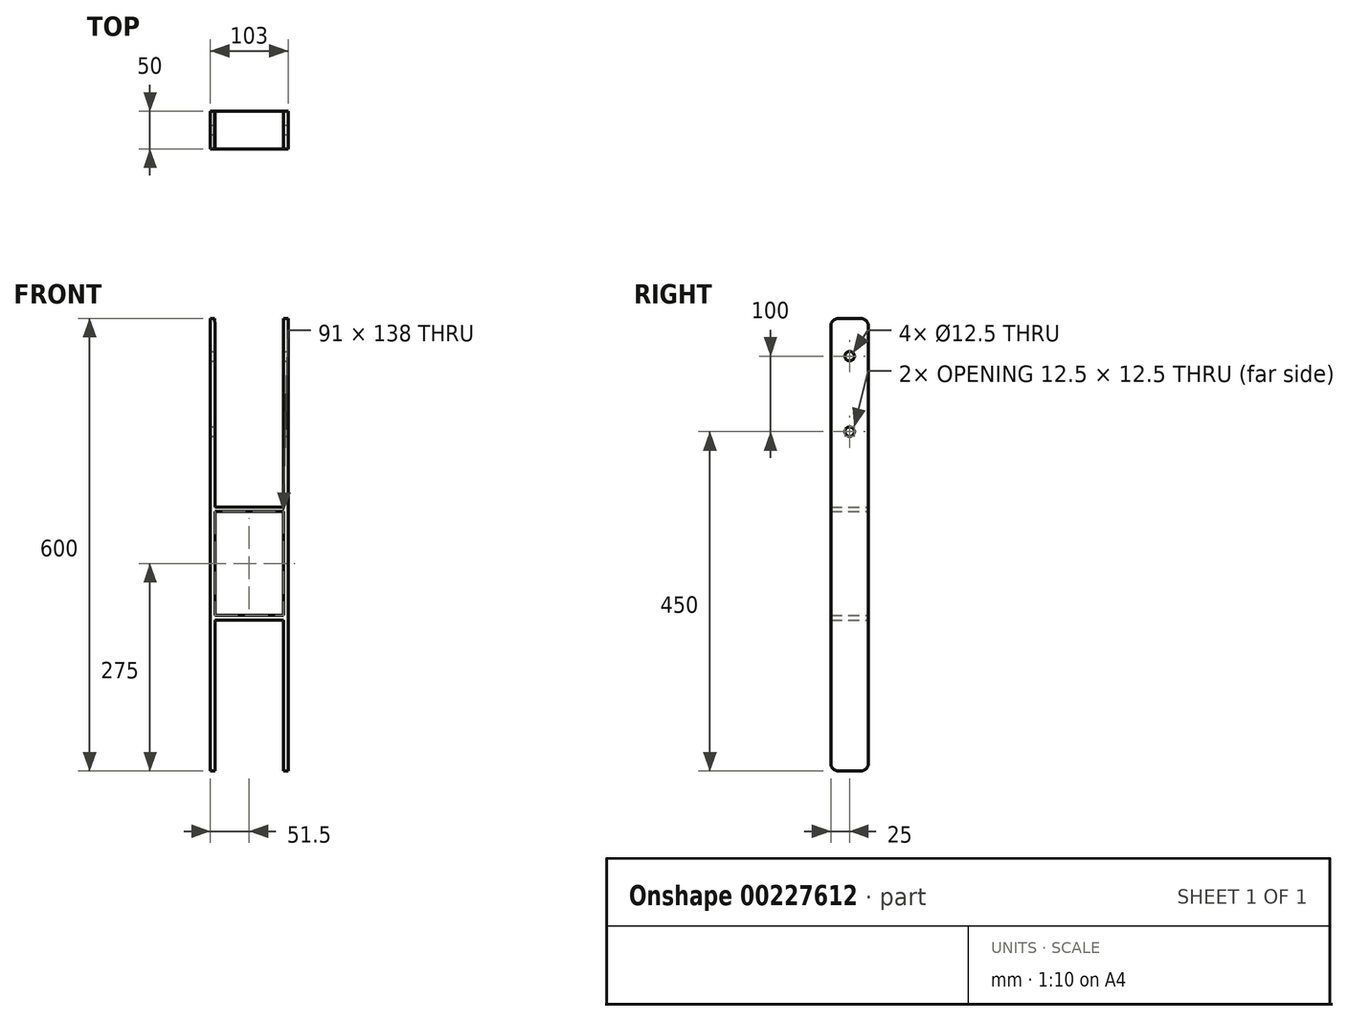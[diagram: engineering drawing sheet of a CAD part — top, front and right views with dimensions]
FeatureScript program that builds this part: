
annotation { "Feature Type Name" : "Feature", "Feature Type Description" : "" }
export const myFeature = defineFeature(function(context is Context, id is Id, definition is map)
    precondition{}
    {
        {
            var Q0;
            Q0=qCreatedBy(makeId("Front.planeOp"),FACE);
            var sketch = newSketch(context, id + "F0", { "sketchPlane" : qUnion([Q0])});
            skLineSegment(sketch, "E0", {"start": v(-200.62, 0) * mm, "end": v(200.75, 0) * mm, "construction": true});
            skLineSegment(sketch, "E1", {"start": v(0, -177.39) * mm, "end": v(0, 159.8) * mm, "construction": true});
            skLineSegment(sketch, "E2", {"start": v(-45.5, 0) * mm, "end": v(45.5, 0) * mm});
            skLineSegment(sketch, "E3", {"start": v(45.5, 0) * mm, "end": v(45.5, 250) * mm});
            skLineSegment(sketch, "E4", {"start": v(45.5, 250) * mm, "end": v(51.5, 250) * mm});
            skLineSegment(sketch, "E5", {"start": v(51.5, 250) * mm, "end": v(51.5, -350) * mm});
            skLineSegment(sketch, "E6", {"start": v(51.5, -350) * mm, "end": v(45.5, -350) * mm});
            skLineSegment(sketch, "E7", {"start": v(45.5, -350) * mm, "end": v(45.5, -150) * mm});
            skLineSegment(sketch, "E8", {"start": v(45.5, -150) * mm, "end": v(-45.5, -150) * mm});
            skLineSegment(sketch, "E9", {"start": v(-45.5, -150) * mm, "end": v(-45.5, -350) * mm});
            skLineSegment(sketch, "E10", {"start": v(-45.5, -350) * mm, "end": v(-51.5, -350) * mm});
            skLineSegment(sketch, "E11", {"start": v(-51.5, -350) * mm, "end": v(-51.5, 250) * mm});
            skLineSegment(sketch, "E12", {"start": v(-51.5, 250) * mm, "end": v(-45.7, 250) * mm});
            skLineSegment(sketch, "E13", {"start": v(-45.7, 250) * mm, "end": v(-45.5, 0) * mm});
            skLineSegment(sketch, "E14.bottom", {"start": v(-45.5, -6) * mm, "end": v(45.5, -6) * mm});
            skLineSegment(sketch, "E14.top", {"start": v(-45.5, -144) * mm, "end": v(45.5, -144) * mm});
            skLineSegment(sketch, "E14.left", {"start": v(-45.5, -6) * mm, "end": v(-45.5, -144) * mm});
            skLineSegment(sketch, "E14.right", {"start": v(45.5, -6) * mm, "end": v(45.5, -144) * mm});
            skSolve(sketch);
        }
        {
            var Q0;
            Q0 = qSketchRegion(id + "F0", true);
            extrude(context, id + "F1", {"entities" : qUnion([Q0]), "endBound" : BoundingType.SYMMETRIC, "depth" : 50 * mm});
        }
        {
            var Q0;
            Q0=makeQuery(id+"F1.opExtrude","CAP_EDGE",EDGE,{"disambiguationData":[OSD([sQuery(id+"F0.wireOp",EDGE,"E4")])],"isStart":false});
            var Q1;
            Q1=makeQuery(id+"F1.opExtrude","CAP_EDGE",EDGE,{"disambiguationData":[OSD([sQuery(id+"F0.wireOp",EDGE,"E4")])],"isStart":true});
            var Q2;
            Q2=makeQuery(id+"F1.opExtrude","CAP_EDGE",EDGE,{"disambiguationData":[OSD([sQuery(id+"F0.wireOp",EDGE,"E12")])],"isStart":false});
            var Q3;
            Q3=makeQuery(id+"F1.opExtrude","CAP_EDGE",EDGE,{"disambiguationData":[OSD([sQuery(id+"F0.wireOp",EDGE,"E12")])],"isStart":true});
            var Q4;
            Q4=makeQuery(id+"F1.opExtrude","CAP_EDGE",EDGE,{"disambiguationData":[OSD([sQuery(id+"F0.wireOp",EDGE,"E6")])],"isStart":false});
            var Q5;
            Q5=makeQuery(id+"F1.opExtrude","CAP_EDGE",EDGE,{"disambiguationData":[OSD([sQuery(id+"F0.wireOp",EDGE,"E10")])],"isStart":false});
            var Q6;
            Q6=makeQuery(id+"F1.opExtrude","CAP_EDGE",EDGE,{"disambiguationData":[OSD([sQuery(id+"F0.wireOp",EDGE,"E6")])],"isStart":true});
            var Q7;
            Q7=makeQuery(id+"F1.opExtrude","CAP_EDGE",EDGE,{"disambiguationData":[OSD([sQuery(id+"F0.wireOp",EDGE,"E10")])],"isStart":true});
            fillet(context, id + "F2", {"entities" : qUnion([Q0, Q1, Q2, Q3, Q4, Q5, Q6, Q7]), "radius" : 10 * mm, "tangentPropagation" : true, "allowEdgeOverflow" : false});
        }
        {
            var Q0;
            Q0=makeQuery(id+"F1.opExtrude","SWEPT_FACE",FACE,{"disambiguationData":[OSD([sQuery(id+"F0.wireOp",EDGE,"E5")])]});
            var sketch = newSketch(context, id + "F3", { "sketchPlane" : qUnion([Q0])});
            skLineSegment(sketch, "E15", {"start": v(0, 0) * mm, "end": v(0, 250) * mm, "construction": true});
            skCircle(sketch, "E16", {"center": v(0, 200) * mm, "radius": 6.25 * mm});
            skCircle(sketch, "E17", {"center": v(0, 100) * mm, "radius": 6.25 * mm});
            skSolve(sketch);
        }
        {
            var Q0;
            Q0 = qSketchRegion(id + "F3", true);
            extrude(context, id + "F4", {"entities" : qUnion([Q0]), "operationType" : NewBodyOperationType.REMOVE, "endBound" : BoundingType.THROUGH_ALL, "oppositeDirection" : true, "depth" : 25 * mm});
        }
    });
